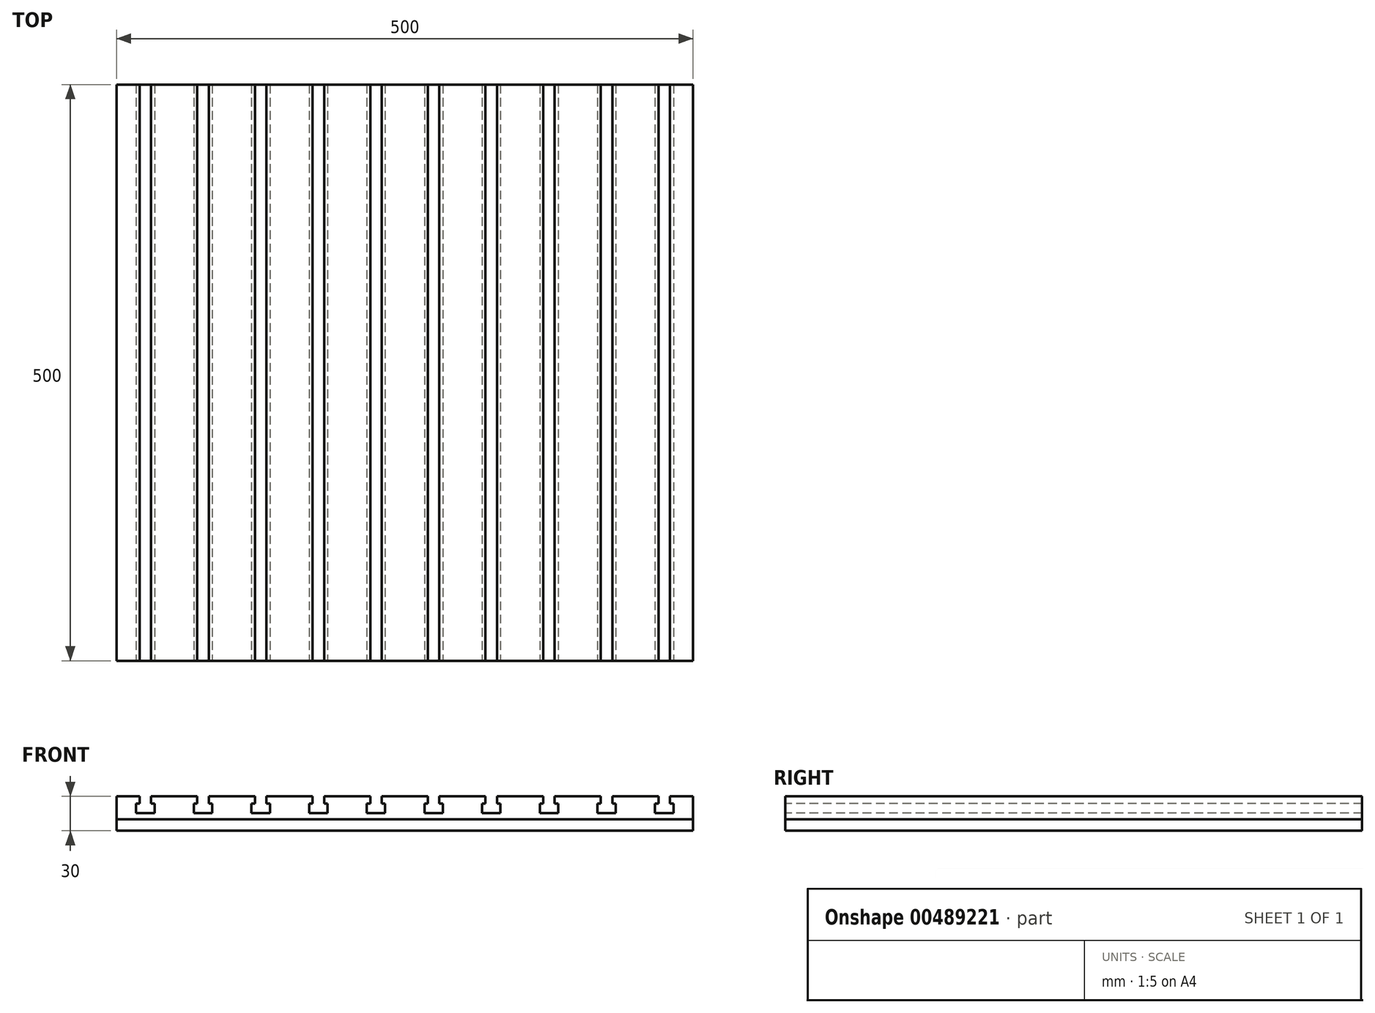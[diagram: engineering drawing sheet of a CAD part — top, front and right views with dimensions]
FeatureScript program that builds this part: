
annotation { "Feature Type Name" : "Feature", "Feature Type Description" : "" }
export const myFeature = defineFeature(function(context is Context, id is Id, definition is map)
    precondition{}
    {
        {
            var Q0;
            Q0=qCreatedBy(makeId("Front.planeOp"),FACE);
            var sketch = newSketch(context, id + "F0", { "sketchPlane" : qUnion([Q0])});
            skLineSegment(sketch, "E0.bottom", {"start": v(-5.17, 10) * mm, "end": v(494.83, 10) * mm});
            skLineSegment(sketch, "E0.top", {"start": v(-5.17, 30) * mm, "end": v(14.83, 30) * mm});
            skLineSegment(sketch, "E0.left", {"start": v(-5.17, 10) * mm, "end": v(-5.17, 30) * mm});
            skLineSegment(sketch, "E0.right", {"start": v(494.83, 10) * mm, "end": v(494.83, 30) * mm});
            skLineSegment(sketch, "E1.left", {"start": v(14.83, 30) * mm, "end": v(14.83, 23.5) * mm});
            skLineSegment(sketch, "E1.right", {"start": v(24.83, 30) * mm, "end": v(24.83, 23.5) * mm});
            skLineSegment(sketch, "E2.bottom", {"start": v(11.83, 23.5) * mm, "end": v(14.83, 23.5) * mm});
            skLineSegment(sketch, "E2.top", {"start": v(11.83, 15.5) * mm, "end": v(27.83, 15.5) * mm});
            skLineSegment(sketch, "E2.left", {"start": v(11.83, 23.5) * mm, "end": v(11.83, 15.5) * mm});
            skLineSegment(sketch, "E2.right", {"start": v(27.83, 23.5) * mm, "end": v(27.83, 15.5) * mm});
            skPoint(sketch, "E3", {"position": v(19.83, 23.5) * mm});
            skLineSegment(sketch, "E4.trimOffspring", {"start": v(24.83, 30) * mm, "end": v(64.83, 30) * mm});
            skLineSegment(sketch, "E5.trimOffspring", {"start": v(24.83, 23.5) * mm, "end": v(27.83, 23.5) * mm});
            skPoint(sketch, "E6.1.0.0", {"position": v(69.83, 23.5) * mm});
            skLineSegment(sketch, "E6.1.0.1", {"start": v(61.83, 15.5) * mm, "end": v(77.83, 15.5) * mm});
            skLineSegment(sketch, "E6.1.0.2", {"start": v(77.83, 23.5) * mm, "end": v(77.83, 15.5) * mm});
            skLineSegment(sketch, "E6.1.0.3", {"start": v(61.83, 23.5) * mm, "end": v(61.83, 15.5) * mm});
            skLineSegment(sketch, "E6.1.0.4", {"start": v(64.83, 30) * mm, "end": v(64.83, 23.5) * mm});
            skLineSegment(sketch, "E6.1.0.5", {"start": v(74.83, 30) * mm, "end": v(74.83, 23.5) * mm});
            skLineSegment(sketch, "E6.1.0.6", {"start": v(61.83, 23.5) * mm, "end": v(64.83, 23.5) * mm});
            skLineSegment(sketch, "E6.1.0.7", {"start": v(74.83, 23.5) * mm, "end": v(77.83, 23.5) * mm});
            skPoint(sketch, "E6.2.0.0", {"position": v(119.83, 23.5) * mm});
            skLineSegment(sketch, "E6.2.0.1", {"start": v(111.83, 15.5) * mm, "end": v(127.83, 15.5) * mm});
            skLineSegment(sketch, "E6.2.0.2", {"start": v(127.83, 23.5) * mm, "end": v(127.83, 15.5) * mm});
            skLineSegment(sketch, "E6.2.0.3", {"start": v(111.83, 23.5) * mm, "end": v(111.83, 15.5) * mm});
            skLineSegment(sketch, "E6.2.0.4", {"start": v(114.83, 30) * mm, "end": v(114.83, 23.5) * mm});
            skLineSegment(sketch, "E6.2.0.5", {"start": v(124.83, 30) * mm, "end": v(124.83, 23.5) * mm});
            skLineSegment(sketch, "E6.2.0.6", {"start": v(111.83, 23.5) * mm, "end": v(114.83, 23.5) * mm});
            skLineSegment(sketch, "E6.2.0.7", {"start": v(124.83, 23.5) * mm, "end": v(127.83, 23.5) * mm});
            skPoint(sketch, "E6.3.0.0", {"position": v(169.83, 23.5) * mm});
            skLineSegment(sketch, "E6.3.0.1", {"start": v(161.83, 15.5) * mm, "end": v(177.83, 15.5) * mm});
            skLineSegment(sketch, "E6.3.0.2", {"start": v(177.83, 23.5) * mm, "end": v(177.83, 15.5) * mm});
            skLineSegment(sketch, "E6.3.0.3", {"start": v(161.83, 23.5) * mm, "end": v(161.83, 15.5) * mm});
            skLineSegment(sketch, "E6.3.0.4", {"start": v(164.83, 30) * mm, "end": v(164.83, 23.5) * mm});
            skLineSegment(sketch, "E6.3.0.5", {"start": v(174.83, 30) * mm, "end": v(174.83, 23.5) * mm});
            skLineSegment(sketch, "E6.3.0.6", {"start": v(161.83, 23.5) * mm, "end": v(164.83, 23.5) * mm});
            skLineSegment(sketch, "E6.3.0.7", {"start": v(174.83, 23.5) * mm, "end": v(177.83, 23.5) * mm});
            skPoint(sketch, "E6.4.0.0", {"position": v(219.83, 23.5) * mm});
            skLineSegment(sketch, "E6.4.0.1", {"start": v(211.83, 15.5) * mm, "end": v(227.83, 15.5) * mm});
            skLineSegment(sketch, "E6.4.0.2", {"start": v(227.83, 23.5) * mm, "end": v(227.83, 15.5) * mm});
            skLineSegment(sketch, "E6.4.0.3", {"start": v(211.83, 23.5) * mm, "end": v(211.83, 15.5) * mm});
            skLineSegment(sketch, "E6.4.0.4", {"start": v(214.83, 30) * mm, "end": v(214.83, 23.5) * mm});
            skLineSegment(sketch, "E6.4.0.5", {"start": v(224.83, 30) * mm, "end": v(224.83, 23.5) * mm});
            skLineSegment(sketch, "E6.4.0.6", {"start": v(211.83, 23.5) * mm, "end": v(214.83, 23.5) * mm});
            skLineSegment(sketch, "E6.4.0.7", {"start": v(224.83, 23.5) * mm, "end": v(227.83, 23.5) * mm});
            skPoint(sketch, "E6.5.0.0", {"position": v(269.83, 23.5) * mm});
            skLineSegment(sketch, "E6.5.0.1", {"start": v(261.83, 15.5) * mm, "end": v(277.83, 15.5) * mm});
            skLineSegment(sketch, "E6.5.0.2", {"start": v(277.83, 23.5) * mm, "end": v(277.83, 15.5) * mm});
            skLineSegment(sketch, "E6.5.0.3", {"start": v(261.83, 23.5) * mm, "end": v(261.83, 15.5) * mm});
            skLineSegment(sketch, "E6.5.0.4", {"start": v(264.83, 30) * mm, "end": v(264.83, 23.5) * mm});
            skLineSegment(sketch, "E6.5.0.5", {"start": v(274.83, 30) * mm, "end": v(274.83, 23.5) * mm});
            skLineSegment(sketch, "E6.5.0.6", {"start": v(261.83, 23.5) * mm, "end": v(264.83, 23.5) * mm});
            skLineSegment(sketch, "E6.5.0.7", {"start": v(274.83, 23.5) * mm, "end": v(277.83, 23.5) * mm});
            skPoint(sketch, "E6.6.0.0", {"position": v(319.83, 23.5) * mm});
            skLineSegment(sketch, "E6.6.0.1", {"start": v(311.83, 15.5) * mm, "end": v(327.83, 15.5) * mm});
            skLineSegment(sketch, "E6.6.0.2", {"start": v(327.83, 23.5) * mm, "end": v(327.83, 15.5) * mm});
            skLineSegment(sketch, "E6.6.0.3", {"start": v(311.83, 23.5) * mm, "end": v(311.83, 15.5) * mm});
            skLineSegment(sketch, "E6.6.0.4", {"start": v(314.83, 30) * mm, "end": v(314.83, 23.5) * mm});
            skLineSegment(sketch, "E6.6.0.5", {"start": v(324.83, 30) * mm, "end": v(324.83, 23.5) * mm});
            skLineSegment(sketch, "E6.6.0.6", {"start": v(311.83, 23.5) * mm, "end": v(314.83, 23.5) * mm});
            skLineSegment(sketch, "E6.6.0.7", {"start": v(324.83, 23.5) * mm, "end": v(327.83, 23.5) * mm});
            skPoint(sketch, "E6.7.0.0", {"position": v(369.83, 23.5) * mm});
            skLineSegment(sketch, "E6.7.0.1", {"start": v(361.83, 15.5) * mm, "end": v(377.83, 15.5) * mm});
            skLineSegment(sketch, "E6.7.0.2", {"start": v(377.83, 23.5) * mm, "end": v(377.83, 15.5) * mm});
            skLineSegment(sketch, "E6.7.0.3", {"start": v(361.83, 23.5) * mm, "end": v(361.83, 15.5) * mm});
            skLineSegment(sketch, "E6.7.0.4", {"start": v(364.83, 30) * mm, "end": v(364.83, 23.5) * mm});
            skLineSegment(sketch, "E6.7.0.5", {"start": v(374.83, 30) * mm, "end": v(374.83, 23.5) * mm});
            skLineSegment(sketch, "E6.7.0.6", {"start": v(361.83, 23.5) * mm, "end": v(364.83, 23.5) * mm});
            skLineSegment(sketch, "E6.7.0.7", {"start": v(374.83, 23.5) * mm, "end": v(377.83, 23.5) * mm});
            skPoint(sketch, "E6.8.0.0", {"position": v(419.83, 23.5) * mm});
            skLineSegment(sketch, "E6.8.0.1", {"start": v(411.83, 15.5) * mm, "end": v(427.83, 15.5) * mm});
            skLineSegment(sketch, "E6.8.0.2", {"start": v(427.83, 23.5) * mm, "end": v(427.83, 15.5) * mm});
            skLineSegment(sketch, "E6.8.0.3", {"start": v(411.83, 23.5) * mm, "end": v(411.83, 15.5) * mm});
            skLineSegment(sketch, "E6.8.0.4", {"start": v(414.83, 30) * mm, "end": v(414.83, 23.5) * mm});
            skLineSegment(sketch, "E6.8.0.5", {"start": v(424.83, 30) * mm, "end": v(424.83, 23.5) * mm});
            skLineSegment(sketch, "E6.8.0.6", {"start": v(411.83, 23.5) * mm, "end": v(414.83, 23.5) * mm});
            skLineSegment(sketch, "E6.8.0.7", {"start": v(424.83, 23.5) * mm, "end": v(427.83, 23.5) * mm});
            skPoint(sketch, "E6.9.0.0", {"position": v(469.83, 23.5) * mm});
            skLineSegment(sketch, "E6.9.0.1", {"start": v(461.83, 15.5) * mm, "end": v(477.83, 15.5) * mm});
            skLineSegment(sketch, "E6.9.0.2", {"start": v(477.83, 23.5) * mm, "end": v(477.83, 15.5) * mm});
            skLineSegment(sketch, "E6.9.0.3", {"start": v(461.83, 23.5) * mm, "end": v(461.83, 15.5) * mm});
            skLineSegment(sketch, "E6.9.0.4", {"start": v(464.83, 30) * mm, "end": v(464.83, 23.5) * mm});
            skLineSegment(sketch, "E6.9.0.5", {"start": v(474.83, 30) * mm, "end": v(474.83, 23.5) * mm});
            skLineSegment(sketch, "E6.9.0.6", {"start": v(461.83, 23.5) * mm, "end": v(464.83, 23.5) * mm});
            skLineSegment(sketch, "E6.9.0.7", {"start": v(474.83, 23.5) * mm, "end": v(477.83, 23.5) * mm});
            skLineSegment(sketch, "E6.direction1", {"start": v(11.83, 15.5) * mm, "end": v(61.83, 15.5) * mm, "construction": true});
            skLineSegment(sketch, "E7.trimOffspring", {"start": v(74.83, 30) * mm, "end": v(114.83, 30) * mm});
            skLineSegment(sketch, "E8.trimOffspring", {"start": v(124.83, 30) * mm, "end": v(164.83, 30) * mm});
            skLineSegment(sketch, "E9.trimOffspring", {"start": v(174.83, 30) * mm, "end": v(214.83, 30) * mm});
            skLineSegment(sketch, "E10.trimOffspring", {"start": v(224.83, 30) * mm, "end": v(264.83, 30) * mm});
            skLineSegment(sketch, "E11.trimOffspring", {"start": v(274.83, 30) * mm, "end": v(314.83, 30) * mm});
            skLineSegment(sketch, "E12.trimOffspring", {"start": v(324.83, 30) * mm, "end": v(364.83, 30) * mm});
            skLineSegment(sketch, "E13.trimOffspring", {"start": v(374.83, 30) * mm, "end": v(414.83, 30) * mm});
            skLineSegment(sketch, "E14.trimOffspring", {"start": v(424.83, 30) * mm, "end": v(464.83, 30) * mm});
            skLineSegment(sketch, "E15.trimOffspring", {"start": v(474.83, 30) * mm, "end": v(494.83, 30) * mm});
            skLineSegment(sketch, "E16.top", {"start": v(-5.17, 0) * mm, "end": v(494.83, 0) * mm});
            skLineSegment(sketch, "E16.left", {"start": v(-5.17, 10) * mm, "end": v(-5.17, 0) * mm});
            skLineSegment(sketch, "E16.right", {"start": v(494.83, 10) * mm, "end": v(494.83, 0) * mm});
            skSolve(sketch);
        }
        {
            var Q0;
            Q0=makeQuery(id+"F0.imprint","IMPRINT",FACE,{"disambiguationData":[TD([[makeQuery(id+"F0.imprint","IMPRINT",EDGE,{"derivedFrom":sQuery(id+"F0.wireOp",EDGE,"E0.top")}),-1.0]])]});
            extrude(context, id + "F1", {"entities" : qUnion([Q0]), "oppositeDirection" : true, "depth" : 500 * mm, "offsetDistance" : 25 * mm});
        }
        {
            var Q0;
            Q0=makeQuery(id+"F0.imprint","IMPRINT",FACE,{"disambiguationData":[TD([[makeQuery(id+"F0.imprint","IMPRINT",EDGE,{"derivedFrom":sQuery(id+"F0.wireOp",EDGE,"E0.bottom")}),-1.0]])]});
            extrude(context, id + "F2", {"entities" : qUnion([Q0]), "oppositeDirection" : true, "depth" : 500 * mm, "offsetDistance" : 25 * mm});
        }
    });
